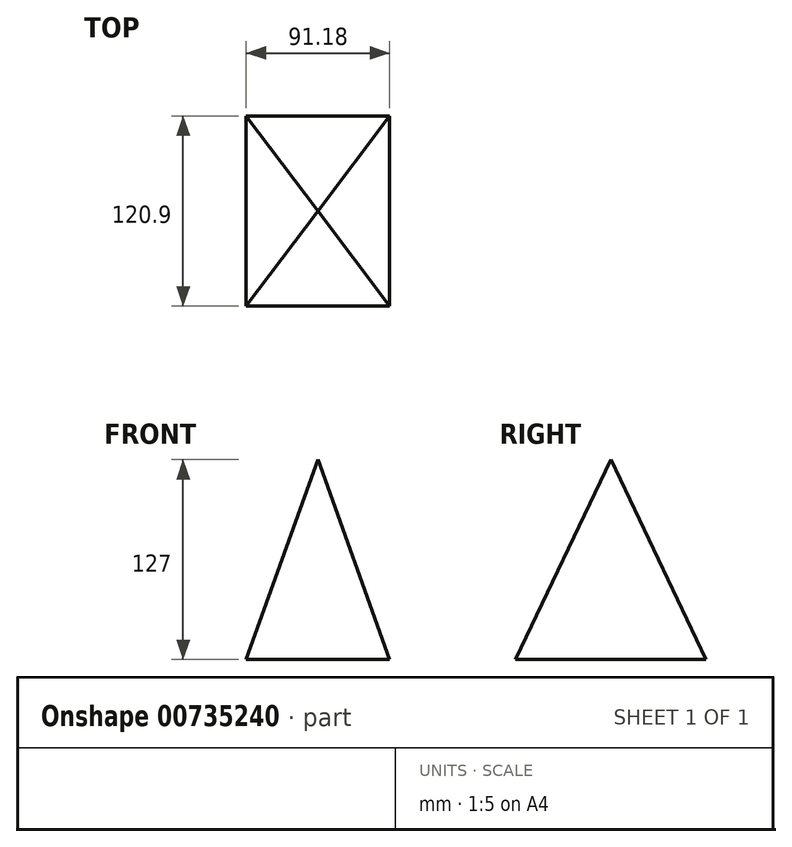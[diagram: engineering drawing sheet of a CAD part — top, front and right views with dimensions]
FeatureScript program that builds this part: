
annotation { "Feature Type Name" : "Feature", "Feature Type Description" : "" }
export const myFeature = defineFeature(function(context is Context, id is Id, definition is map)
    precondition{}
    {
        {
            var Q0;
            Q0=qCreatedBy(makeId("Top.planeOp"),FACE);
            var sketch = newSketch(context, id + "F0", { "sketchPlane" : qUnion([Q0])});
            skLineSegment(sketch, "E0.bottom", {"start": v(45.59, 60.45) * mm, "end": v(-45.59, 60.45) * mm});
            skLineSegment(sketch, "E0.top", {"start": v(45.59, -60.45) * mm, "end": v(-45.59, -60.45) * mm});
            skLineSegment(sketch, "E0.left", {"start": v(45.59, 60.45) * mm, "end": v(45.59, -60.45) * mm});
            skLineSegment(sketch, "E0.right", {"start": v(-45.59, 60.45) * mm, "end": v(-45.59, -60.45) * mm});
            skPoint(sketch, "E0.middle", {"position": v(0, 0) * mm});
            skSolve(sketch);
        }
        {
            var Q0;
            Q0=qCreatedBy(makeId("Top.planeOp"),FACE);
            cPlane(context, id + "F1", {"entities" : qUnion([Q0]), "cplaneType" : CPlaneType.OFFSET, "offset" : 127 * mm, "width" : 152.4 * mm, "height" : 152.4 * mm});
        }
        {
            var Q0;
            Q0=qCreatedBy(id+"F1.planeOp",FACE);
            var sketch = newSketch(context, id + "F2", { "sketchPlane" : qUnion([Q0])});
            skPoint(sketch, "E1.middle", {"position": v(0, 0) * mm});
            skCircle(sketch, "E2", {"center": v(0, 0) * mm, "radius": 31.3 * mm});
            skSolve(sketch);
        }
        {
            var Q0;
            Q0=makeQuery(id+"F0.imprint","IMPRINT",FACE,{"disambiguationData":[TD([[makeQuery(id+"F0.imprint","IMPRINT",EDGE,{"derivedFrom":sQuery(id+"F0.wireOp",EDGE,"E0.bottom")}),1.0]])]});
            var Q1;
            Q1=sQuery(id+"F2.wireOp",VERTEX,"E1.middle");
            loft(context, id + "F3", {"sheetProfilesArray" : [{ "sheetProfileEntities" : qUnion([Q0]) }, { "sheetProfileEntities" : qUnion([Q1]) }]});
        }
    });
